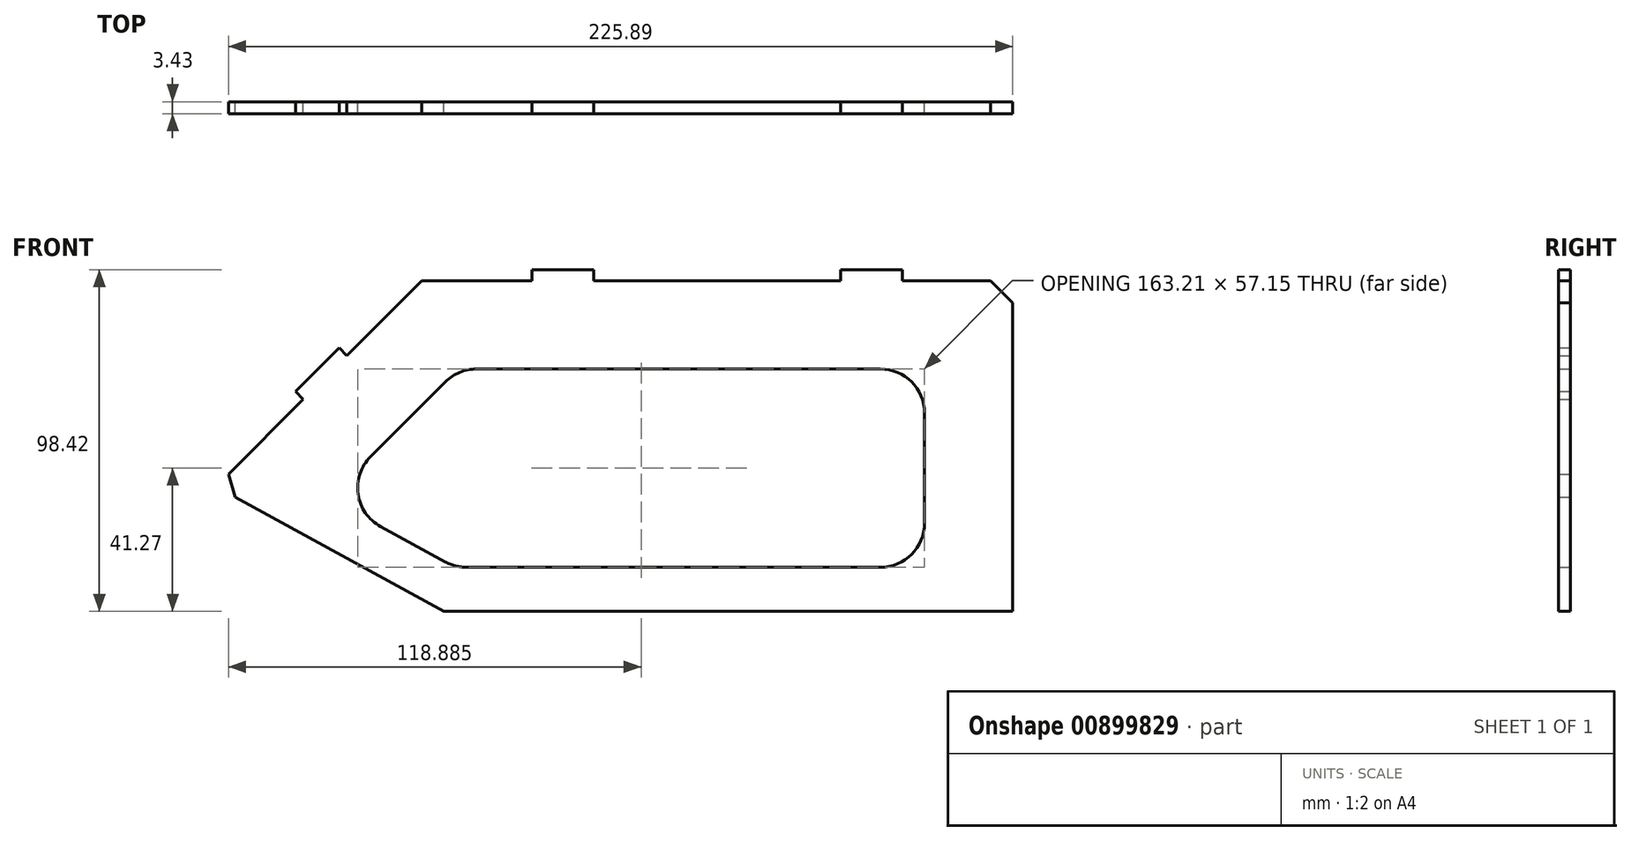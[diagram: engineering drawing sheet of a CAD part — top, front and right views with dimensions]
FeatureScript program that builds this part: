
annotation { "Feature Type Name" : "Feature", "Feature Type Description" : "" }
export const myFeature = defineFeature(function(context is Context, id is Id, definition is map)
    precondition{}
    {
        {
            var Q0;
            Q0=qCreatedBy(makeId("Front.planeOp"),FACE);
            var sketch = newSketch(context, id + "F0", { "sketchPlane" : qUnion([Q0])});
            skArc(sketch, "E0", {"start": v(-421.76, -406.28) * mm, "mid": v(-425.35, -417.06) * mm, "end": v(-418.88, -426.4) * mm});
            skLineSegment(sketch, "E1", {"start": v(-418.88, -426.4) * mm, "end": v(-400.25, -436.59) * mm});
            skArc(sketch, "E2", {"start": v(-400.25, -436.59) * mm, "mid": v(-397.3, -437.75) * mm, "end": v(-394.16, -438.14) * mm});
            skLineSegment(sketch, "E3", {"start": v(-394.16, -438.14) * mm, "end": v(-274.92, -438.14) * mm});
            skArc(sketch, "E4", {"start": v(-274.92, -438.14) * mm, "mid": v(-265.94, -434.42) * mm, "end": v(-262.22, -425.44) * mm});
            skLineSegment(sketch, "E5", {"start": v(-262.22, -425.44) * mm, "end": v(-262.22, -393.7) * mm});
            skArc(sketch, "E6", {"start": v(-262.22, -393.7) * mm, "mid": v(-265.94, -384.71) * mm, "end": v(-274.92, -381) * mm});
            skLineSegment(sketch, "E7", {"start": v(-274.92, -381) * mm, "end": v(-391.22, -381) * mm});
            skArc(sketch, "E8", {"start": v(-391.22, -381) * mm, "mid": v(-396.08, -381.96) * mm, "end": v(-400.2, -384.71) * mm});
            skLineSegment(sketch, "E9", {"start": v(-400.2, -384.71) * mm, "end": v(-421.76, -406.28) * mm});
            skLineSegment(sketch, "E10", {"start": v(-375.25, -352.42) * mm, "end": v(-375.25, -355.6) * mm});
            skLineSegment(sketch, "E11", {"start": v(-357.47, -352.42) * mm, "end": v(-375.25, -352.42) * mm});
            skLineSegment(sketch, "E12", {"start": v(-357.47, -355.6) * mm, "end": v(-357.47, -352.42) * mm});
            skLineSegment(sketch, "E13", {"start": v(-286.35, -352.42) * mm, "end": v(-286.35, -355.6) * mm});
            skLineSegment(sketch, "E14", {"start": v(-268.57, -352.42) * mm, "end": v(-286.35, -352.42) * mm});
            skLineSegment(sketch, "E15", {"start": v(-268.57, -355.6) * mm, "end": v(-268.57, -352.42) * mm});
            skLineSegment(sketch, "E16", {"start": v(-236.82, -361.94) * mm, "end": v(-243.17, -355.6) * mm});
            skLineSegment(sketch, "E17", {"start": v(-400.65, -450.84) * mm, "end": v(-460.76, -417.97) * mm});
            skLineSegment(sketch, "E18", {"start": v(-462.7, -411.3) * mm, "end": v(-460.76, -417.97) * mm});
            skLineSegment(sketch, "E19", {"start": v(-443.39, -387.5) * mm, "end": v(-441.14, -389.74) * mm});
            skLineSegment(sketch, "E20", {"start": v(-430.81, -374.92) * mm, "end": v(-443.39, -387.5) * mm});
            skLineSegment(sketch, "E21", {"start": v(-428.57, -377.16) * mm, "end": v(-430.81, -374.92) * mm});
            skLineSegment(sketch, "E22", {"start": v(-236.82, -450.84) * mm, "end": v(-236.82, -361.94) * mm});
            skLineSegment(sketch, "E23", {"start": v(-400.65, -450.84) * mm, "end": v(-236.82, -450.84) * mm});
            skLineSegment(sketch, "E24", {"start": v(-407, -355.6) * mm, "end": v(-428.57, -377.16) * mm});
            skLineSegment(sketch, "E25", {"start": v(-375.25, -355.6) * mm, "end": v(-407, -355.6) * mm});
            skLineSegment(sketch, "E26", {"start": v(-286.35, -355.6) * mm, "end": v(-357.47, -355.6) * mm});
            skLineSegment(sketch, "E27", {"start": v(-243.17, -355.6) * mm, "end": v(-268.57, -355.6) * mm});
            skLineSegment(sketch, "E28", {"start": v(-441.14, -389.74) * mm, "end": v(-462.7, -411.3) * mm});
            skSolve(sketch);
        }
        {
            var Q0;
            Q0 = qSketchRegion(id + "F0", true);
            extrude(context, id + "F1", {"entities" : qUnion([Q0]), "depth" : 3.43 * mm, "offsetDistance" : 25.4 * mm});
        }
    });
